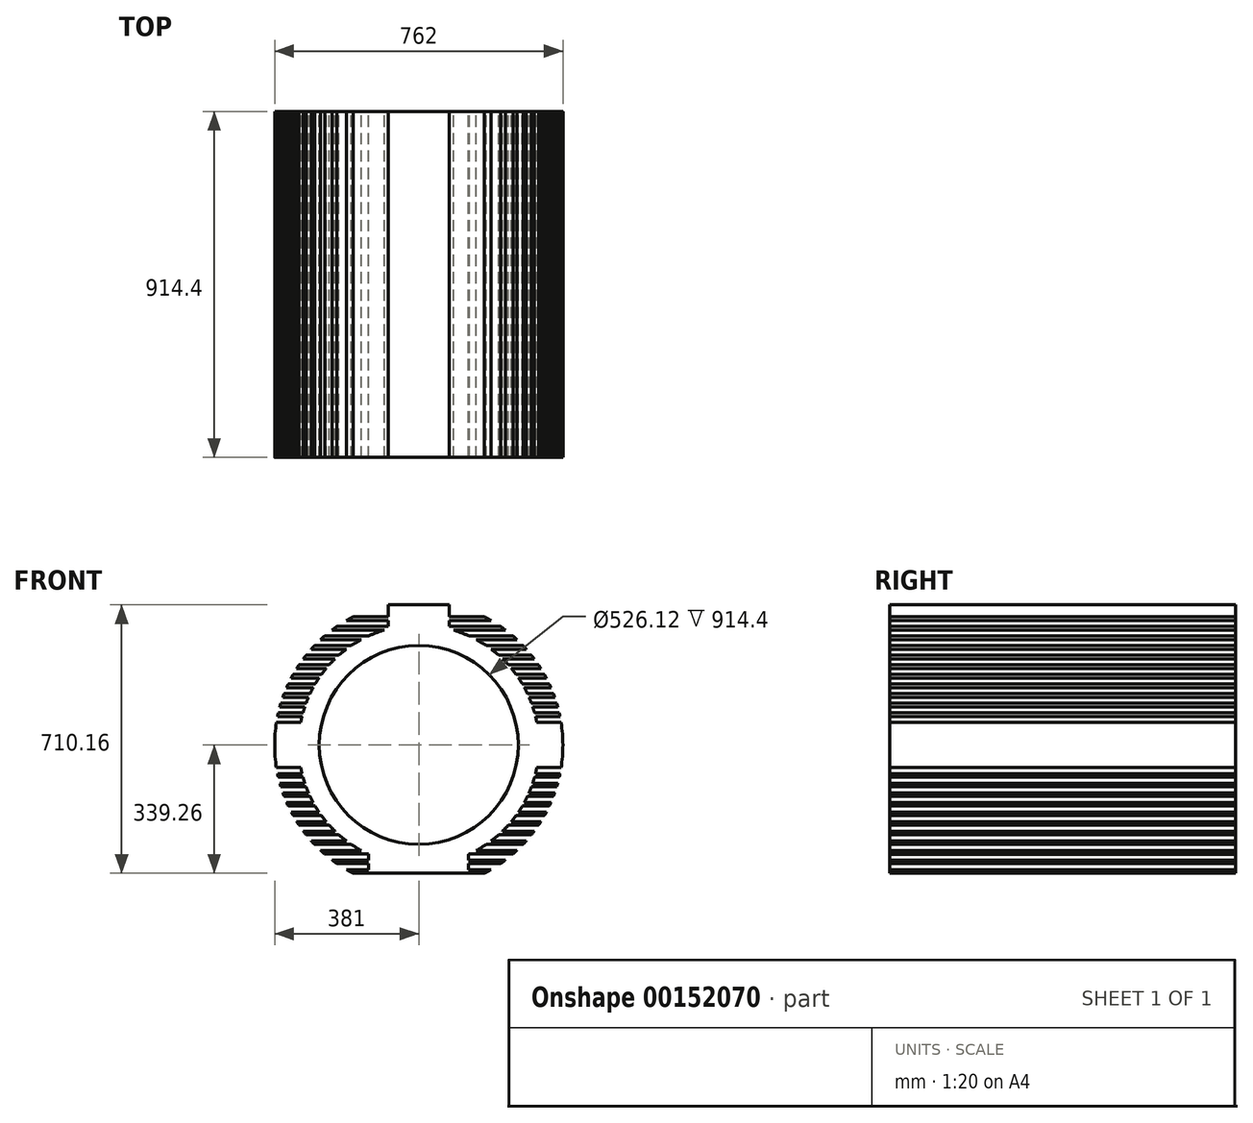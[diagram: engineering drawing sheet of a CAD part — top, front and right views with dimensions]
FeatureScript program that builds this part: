
annotation { "Feature Type Name" : "Feature", "Feature Type Description" : "" }
export const myFeature = defineFeature(function(context is Context, id is Id, definition is map)
    precondition{}
    {
        {
            var Q0;
            Q0=qCreatedBy(makeId("Front.planeOp"),FACE);
            var sketch = newSketch(context, id + "F0", { "sketchPlane" : qUnion([Q0])});
            skArc(sketch, "E0", {"start": v(371.34, -85.26) * mm, "mid": v(372.4, -80.5) * mm, "end": v(373.4, -75.74) * mm});
            skCircle(sketch, "E1", {"center": v(0, 0) * mm, "radius": 317.77 * mm});
            skLineSegment(sketch, "E2.bottom", {"start": v(337.21, 177.34) * mm, "end": v(263.69, 177.34) * mm});
            skLineSegment(sketch, "E2.top", {"start": v(332.03, 186.86) * mm, "end": v(257.02, 186.86) * mm});
            skPoint(sketch, "E2.middle", {"position": v(0, 182.1) * mm});
            skLineSegment(sketch, "E3", {"start": v(0, 470.68) * mm, "end": v(0, -487.75) * mm, "construction": true});
            skLineSegment(sketch, "E4.bottom", {"start": v(322.58, 202.74) * mm, "end": v(244.7, 202.74) * mm});
            skLineSegment(sketch, "E4.top", {"start": v(316.4, 212.26) * mm, "end": v(236.48, 212.26) * mm});
            skLineSegment(sketch, "E5.bottom", {"start": v(305.15, 228.14) * mm, "end": v(221.2, 228.14) * mm});
            skLineSegment(sketch, "E5.top", {"start": v(297.79, 237.66) * mm, "end": v(210.94, 237.66) * mm});
            skLineSegment(sketch, "E6.bottom", {"start": v(284.4, 253.54) * mm, "end": v(191.57, 253.54) * mm});
            skLineSegment(sketch, "E6.top", {"start": v(275.6, 263.06) * mm, "end": v(178.26, 263.06) * mm});
            skLineSegment(sketch, "E7.bottom", {"start": v(259.53, 278.94) * mm, "end": v(152.23, 278.94) * mm});
            skLineSegment(sketch, "E7.top", {"start": v(248.9, 288.46) * mm, "end": v(133.3, 288.46) * mm});
            skLineSegment(sketch, "E8.bottom", {"start": v(229.22, 304.34) * mm, "end": v(91.42, 304.34) * mm});
            skLineSegment(sketch, "E8.top", {"start": v(216, 313.86) * mm, "end": v(80.97, 313.86) * mm});
            skLineSegment(sketch, "E9.bottom", {"start": v(190.88, 329.74) * mm, "end": v(80.97, 329.74) * mm});
            skLineSegment(sketch, "E9.top", {"start": v(173.39, 339.26) * mm, "end": v(80.97, 339.26) * mm});
            skLineSegment(sketch, "E10.bottom", {"start": v(349.4, 151.94) * mm, "end": v(279.1, 151.94) * mm});
            skLineSegment(sketch, "E10.top", {"start": v(345.1, 161.46) * mm, "end": v(273.7, 161.46) * mm});
            skLineSegment(sketch, "E11.bottom", {"start": v(359.37, 126.54) * mm, "end": v(291.5, 126.54) * mm});
            skLineSegment(sketch, "E11.top", {"start": v(355.88, 136.06) * mm, "end": v(287.17, 136.06) * mm});
            skLineSegment(sketch, "E12.bottom", {"start": v(367.33, 101.14) * mm, "end": v(301.25, 101.14) * mm});
            skLineSegment(sketch, "E12.top", {"start": v(364.58, 110.66) * mm, "end": v(297.88, 110.66) * mm});
            skLineSegment(sketch, "E13.bottom", {"start": v(373.4, 75.74) * mm, "end": v(308.61, 75.74) * mm});
            skLineSegment(sketch, "E13.top", {"start": v(371.34, 85.26) * mm, "end": v(306.12, 85.26) * mm});
            skLineSegment(sketch, "E14.trimOffspring", {"start": v(-308.61, 75.74) * mm, "end": v(-373.4, 75.74) * mm});
            skLineSegment(sketch, "E15.trimOffspring", {"start": v(-306.12, 85.26) * mm, "end": v(-371.34, 85.26) * mm});
            skLineSegment(sketch, "E16.trimOffspring", {"start": v(-301.25, 101.14) * mm, "end": v(-367.33, 101.14) * mm});
            skLineSegment(sketch, "E17.trimOffspring", {"start": v(-297.88, 110.66) * mm, "end": v(-364.58, 110.66) * mm});
            skLineSegment(sketch, "E18.trimOffspring", {"start": v(-291.5, 126.54) * mm, "end": v(-359.37, 126.54) * mm});
            skLineSegment(sketch, "E19.trimOffspring", {"start": v(-287.17, 136.06) * mm, "end": v(-355.88, 136.06) * mm});
            skLineSegment(sketch, "E20.trimOffspring", {"start": v(-279.1, 151.94) * mm, "end": v(-349.4, 151.94) * mm});
            skLineSegment(sketch, "E21.trimOffspring", {"start": v(-273.7, 161.46) * mm, "end": v(-345.1, 161.46) * mm});
            skLineSegment(sketch, "E22.trimOffspring", {"start": v(-263.69, 177.34) * mm, "end": v(-337.21, 177.34) * mm});
            skLineSegment(sketch, "E23.trimOffspring", {"start": v(-257.02, 186.86) * mm, "end": v(-332.03, 186.86) * mm});
            skLineSegment(sketch, "E24.trimOffspring", {"start": v(-244.7, 202.74) * mm, "end": v(-322.58, 202.74) * mm});
            skLineSegment(sketch, "E25.trimOffspring", {"start": v(-236.48, 212.26) * mm, "end": v(-316.4, 212.26) * mm});
            skLineSegment(sketch, "E26.trimOffspring", {"start": v(-221.2, 228.14) * mm, "end": v(-305.15, 228.14) * mm});
            skLineSegment(sketch, "E27.trimOffspring", {"start": v(-210.94, 237.66) * mm, "end": v(-297.79, 237.66) * mm});
            skLineSegment(sketch, "E28.trimOffspring", {"start": v(-191.57, 253.54) * mm, "end": v(-284.4, 253.54) * mm});
            skLineSegment(sketch, "E29.trimOffspring", {"start": v(-178.26, 263.06) * mm, "end": v(-275.6, 263.06) * mm});
            skLineSegment(sketch, "E30.trimOffspring", {"start": v(-152.23, 278.94) * mm, "end": v(-259.53, 278.94) * mm});
            skLineSegment(sketch, "E31.trimOffspring", {"start": v(-133.3, 288.46) * mm, "end": v(-248.9, 288.46) * mm});
            skLineSegment(sketch, "E32.trimOffspring", {"start": v(-91.42, 304.34) * mm, "end": v(-229.22, 304.34) * mm});
            skLineSegment(sketch, "E33.trimOffspring", {"start": v(-80.97, 313.86) * mm, "end": v(-216, 313.86) * mm});
            skLineSegment(sketch, "E34", {"start": v(-457.72, 0) * mm, "end": v(505.35, 0) * mm, "construction": true});
            skLineSegment(sketch, "E35.MirrorCS", {"start": v(345.1, -161.46) * mm, "end": v(273.7, -161.46) * mm});
            skLineSegment(sketch, "E36.MirrorCS", {"start": v(-178.26, -263.06) * mm, "end": v(-275.6, -263.06) * mm});
            skLineSegment(sketch, "E37.MirrorCS", {"start": v(-263.69, -177.34) * mm, "end": v(-337.21, -177.34) * mm});
            skLineSegment(sketch, "E38.MirrorCS", {"start": v(-236.48, -212.26) * mm, "end": v(-316.4, -212.26) * mm});
            skLineSegment(sketch, "E39.MirrorCS", {"start": v(-291.5, -126.54) * mm, "end": v(-359.37, -126.54) * mm});
            skLineSegment(sketch, "E40.MirrorCS", {"start": v(-273.7, -161.46) * mm, "end": v(-345.1, -161.46) * mm});
            skPoint(sketch, "E41.MirrorP", {"position": v(0, -182.1) * mm});
            skLineSegment(sketch, "E42.MirrorCS", {"start": v(305.15, -228.14) * mm, "end": v(221.2, -228.14) * mm});
            skLineSegment(sketch, "E43.MirrorCS", {"start": v(-132.08, -313.86) * mm, "end": v(-216, -313.86) * mm});
            skLineSegment(sketch, "E44.MirrorCS", {"start": v(367.33, -101.14) * mm, "end": v(301.25, -101.14) * mm});
            skLineSegment(sketch, "E45.MirrorCS", {"start": v(-297.88, -110.66) * mm, "end": v(-364.58, -110.66) * mm});
            skLineSegment(sketch, "E46.MirrorCS", {"start": v(-257.02, -186.86) * mm, "end": v(-332.03, -186.86) * mm});
            skLineSegment(sketch, "E47.MirrorCS", {"start": v(297.79, -237.66) * mm, "end": v(210.94, -237.66) * mm});
            skLineSegment(sketch, "E48.MirrorCS", {"start": v(284.4, -253.54) * mm, "end": v(191.57, -253.54) * mm});
            skLineSegment(sketch, "E49.MirrorCS", {"start": v(371.34, -85.26) * mm, "end": v(306.12, -85.26) * mm});
            skLineSegment(sketch, "E50.MirrorCS", {"start": v(275.6, -263.06) * mm, "end": v(178.26, -263.06) * mm});
            skLineSegment(sketch, "E51.MirrorCS", {"start": v(-221.2, -228.14) * mm, "end": v(-305.15, -228.14) * mm});
            skLineSegment(sketch, "E52.MirrorCS", {"start": v(355.88, -136.06) * mm, "end": v(287.17, -136.06) * mm});
            skLineSegment(sketch, "E53.MirrorCS", {"start": v(259.53, -278.94) * mm, "end": v(152.23, -278.94) * mm});
            skLineSegment(sketch, "E54.MirrorCS", {"start": v(248.9, -288.46) * mm, "end": v(133.3, -288.46) * mm});
            skLineSegment(sketch, "E55.MirrorCS", {"start": v(-287.17, -136.06) * mm, "end": v(-355.88, -136.06) * mm});
            skLineSegment(sketch, "E56.MirrorCS", {"start": v(173.39, -339.26) * mm, "end": v(-173.39, -339.26) * mm});
            skLineSegment(sketch, "E57.MirrorCS", {"start": v(322.58, -202.74) * mm, "end": v(244.7, -202.74) * mm});
            skLineSegment(sketch, "E58.MirrorCS", {"start": v(332.03, -186.86) * mm, "end": v(257.02, -186.86) * mm});
            skLineSegment(sketch, "E59.MirrorCS", {"start": v(337.21, -177.34) * mm, "end": v(263.69, -177.34) * mm});
            skLineSegment(sketch, "E60.MirrorCS", {"start": v(-308.61, -75.74) * mm, "end": v(-373.4, -75.74) * mm});
            skLineSegment(sketch, "E61.MirrorCS", {"start": v(316.4, -212.26) * mm, "end": v(236.48, -212.26) * mm});
            skLineSegment(sketch, "E62.MirrorCS", {"start": v(373.4, -75.74) * mm, "end": v(308.61, -75.74) * mm});
            skLineSegment(sketch, "E63.MirrorCS", {"start": v(-133.3, -288.46) * mm, "end": v(-248.9, -288.46) * mm});
            skLineSegment(sketch, "E64.MirrorCS", {"start": v(-191.57, -253.54) * mm, "end": v(-284.4, -253.54) * mm});
            skLineSegment(sketch, "E65.MirrorCS", {"start": v(-244.7, -202.74) * mm, "end": v(-322.58, -202.74) * mm});
            skLineSegment(sketch, "E66.MirrorCS", {"start": v(-306.12, -85.26) * mm, "end": v(-371.34, -85.26) * mm});
            skLineSegment(sketch, "E67.MirrorCS", {"start": v(-152.23, -278.94) * mm, "end": v(-259.53, -278.94) * mm});
            skLineSegment(sketch, "E68.MirrorCS", {"start": v(359.37, -126.54) * mm, "end": v(291.5, -126.54) * mm});
            skLineSegment(sketch, "E69.MirrorCS", {"start": v(190.88, -329.74) * mm, "end": v(132.08, -329.74) * mm});
            skLineSegment(sketch, "E70.MirrorCS", {"start": v(349.4, -151.94) * mm, "end": v(279.1, -151.94) * mm});
            skLineSegment(sketch, "E71.MirrorCS", {"start": v(216, -313.86) * mm, "end": v(132.08, -313.86) * mm});
            skLineSegment(sketch, "E72.MirrorCS", {"start": v(229.22, -304.34) * mm, "end": v(132.08, -304.34) * mm});
            skLineSegment(sketch, "E73.MirrorCS", {"start": v(-132.08, -304.34) * mm, "end": v(-229.22, -304.34) * mm});
            skLineSegment(sketch, "E74.MirrorCS", {"start": v(-210.94, -237.66) * mm, "end": v(-297.79, -237.66) * mm});
            skLineSegment(sketch, "E75.MirrorCS", {"start": v(-279.1, -151.94) * mm, "end": v(-349.4, -151.94) * mm});
            skLineSegment(sketch, "E76.MirrorCS", {"start": v(364.58, -110.66) * mm, "end": v(297.88, -110.66) * mm});
            skLineSegment(sketch, "E77.MirrorCS", {"start": v(-301.25, -101.14) * mm, "end": v(-367.33, -101.14) * mm});
            skArc(sketch, "E78.trimOffspring", {"start": v(364.58, -110.66) * mm, "mid": v(365.98, -105.9) * mm, "end": v(367.33, -101.14) * mm});
            skArc(sketch, "E79.trimOffspring", {"start": v(355.88, -136.06) * mm, "mid": v(357.66, -131.31) * mm, "end": v(359.37, -126.54) * mm});
            skArc(sketch, "E80.trimOffspring", {"start": v(345.1, -161.46) * mm, "mid": v(347.28, -156.71) * mm, "end": v(349.4, -151.94) * mm});
            skArc(sketch, "E81.trimOffspring", {"start": v(332.03, -186.86) * mm, "mid": v(334.66, -182.12) * mm, "end": v(337.21, -177.34) * mm});
            skArc(sketch, "E82.trimOffspring", {"start": v(316.4, -212.26) * mm, "mid": v(319.52, -207.52) * mm, "end": v(322.58, -202.74) * mm});
            skArc(sketch, "E83.trimOffspring", {"start": v(297.79, -237.66) * mm, "mid": v(301.5, -232.93) * mm, "end": v(305.15, -228.14) * mm});
            skArc(sketch, "E84.trimOffspring", {"start": v(275.6, -263.06) * mm, "mid": v(280.04, -258.34) * mm, "end": v(284.4, -253.54) * mm});
            skArc(sketch, "E85.trimOffspring", {"start": v(248.9, -288.46) * mm, "mid": v(254.26, -283.75) * mm, "end": v(259.53, -278.94) * mm});
            skArc(sketch, "E86.trimOffspring", {"start": v(216, -313.86) * mm, "mid": v(222.66, -309.17) * mm, "end": v(229.22, -304.34) * mm});
            skArc(sketch, "E87.trimOffspring", {"start": v(173.39, -339.26) * mm, "mid": v(182.2, -334.61) * mm, "end": v(190.88, -329.74) * mm});
            skArc(sketch, "E88.trimOffspring", {"start": v(-229.22, -304.34) * mm, "mid": v(-222.66, -309.17) * mm, "end": v(-216, -313.86) * mm});
            skArc(sketch, "E89.trimOffspring", {"start": v(-259.53, -278.94) * mm, "mid": v(-254.26, -283.75) * mm, "end": v(-248.9, -288.46) * mm});
            skArc(sketch, "E90.trimOffspring", {"start": v(-284.4, -253.54) * mm, "mid": v(-280.04, -258.34) * mm, "end": v(-275.6, -263.06) * mm});
            skArc(sketch, "E91.trimOffspring", {"start": v(-305.15, -228.14) * mm, "mid": v(-301.5, -232.93) * mm, "end": v(-297.79, -237.66) * mm});
            skArc(sketch, "E92.trimOffspring", {"start": v(-322.58, -202.74) * mm, "mid": v(-319.52, -207.52) * mm, "end": v(-316.4, -212.26) * mm});
            skArc(sketch, "E93.trimOffspring", {"start": v(-337.21, -177.34) * mm, "mid": v(-334.66, -182.12) * mm, "end": v(-332.03, -186.86) * mm});
            skArc(sketch, "E94.trimOffspring", {"start": v(-349.4, -151.94) * mm, "mid": v(-347.28, -156.71) * mm, "end": v(-345.1, -161.46) * mm});
            skArc(sketch, "E95.trimOffspring", {"start": v(-359.37, -126.54) * mm, "mid": v(-357.66, -131.31) * mm, "end": v(-355.88, -136.06) * mm});
            skArc(sketch, "E96.trimOffspring", {"start": v(-367.33, -101.14) * mm, "mid": v(-365.98, -105.9) * mm, "end": v(-364.58, -110.66) * mm});
            skArc(sketch, "E97.trimOffspring", {"start": v(-371.34, 85.26) * mm, "mid": v(-372.4, 80.5) * mm, "end": v(-373.4, 75.74) * mm});
            skArc(sketch, "E98.trimOffspring", {"start": v(-364.58, 110.66) * mm, "mid": v(-365.98, 105.9) * mm, "end": v(-367.33, 101.14) * mm});
            skArc(sketch, "E99.trimOffspring", {"start": v(-355.88, 136.06) * mm, "mid": v(-357.66, 131.31) * mm, "end": v(-359.37, 126.54) * mm});
            skArc(sketch, "E100.trimOffspring", {"start": v(-345.1, 161.46) * mm, "mid": v(-347.28, 156.71) * mm, "end": v(-349.4, 151.94) * mm});
            skArc(sketch, "E101.trimOffspring", {"start": v(-332.03, 186.86) * mm, "mid": v(-334.66, 182.12) * mm, "end": v(-337.21, 177.34) * mm});
            skArc(sketch, "E102.trimOffspring", {"start": v(-316.4, 212.26) * mm, "mid": v(-319.52, 207.52) * mm, "end": v(-322.58, 202.74) * mm});
            skArc(sketch, "E103.trimOffspring", {"start": v(-297.79, 237.66) * mm, "mid": v(-301.5, 232.93) * mm, "end": v(-305.15, 228.14) * mm});
            skArc(sketch, "E104.trimOffspring", {"start": v(-275.6, 263.06) * mm, "mid": v(-280.04, 258.34) * mm, "end": v(-284.4, 253.54) * mm});
            skArc(sketch, "E105.trimOffspring", {"start": v(-248.9, 288.46) * mm, "mid": v(-254.26, 283.75) * mm, "end": v(-259.53, 278.94) * mm});
            skArc(sketch, "E106.trimOffspring", {"start": v(-216, 313.86) * mm, "mid": v(-222.66, 309.17) * mm, "end": v(-229.22, 304.34) * mm});
            skArc(sketch, "E107.trimOffspring", {"start": v(-173.39, 339.26) * mm, "mid": v(-182.2, 334.61) * mm, "end": v(-190.88, 329.74) * mm});
            skArc(sketch, "E108.trimOffspring", {"start": v(190.88, 329.74) * mm, "mid": v(182.2, 334.61) * mm, "end": v(173.39, 339.26) * mm});
            skArc(sketch, "E109.trimOffspring", {"start": v(229.22, 304.34) * mm, "mid": v(222.66, 309.17) * mm, "end": v(216, 313.86) * mm});
            skArc(sketch, "E110.trimOffspring", {"start": v(259.53, 278.94) * mm, "mid": v(254.26, 283.75) * mm, "end": v(248.9, 288.46) * mm});
            skArc(sketch, "E111.trimOffspring", {"start": v(284.4, 253.54) * mm, "mid": v(280.04, 258.34) * mm, "end": v(275.6, 263.06) * mm});
            skArc(sketch, "E112.trimOffspring", {"start": v(305.15, 228.14) * mm, "mid": v(301.5, 232.93) * mm, "end": v(297.79, 237.66) * mm});
            skArc(sketch, "E113.trimOffspring", {"start": v(322.58, 202.74) * mm, "mid": v(319.52, 207.52) * mm, "end": v(316.4, 212.26) * mm});
            skArc(sketch, "E114.trimOffspring", {"start": v(337.21, 177.34) * mm, "mid": v(334.66, 182.12) * mm, "end": v(332.03, 186.86) * mm});
            skArc(sketch, "E115.trimOffspring", {"start": v(349.4, 151.94) * mm, "mid": v(347.28, 156.71) * mm, "end": v(345.1, 161.46) * mm});
            skArc(sketch, "E116.trimOffspring", {"start": v(359.37, 126.54) * mm, "mid": v(357.66, 131.31) * mm, "end": v(355.88, 136.06) * mm});
            skArc(sketch, "E117.trimOffspring", {"start": v(367.33, 101.14) * mm, "mid": v(365.98, 105.9) * mm, "end": v(364.58, 110.66) * mm});
            skLineSegment(sketch, "E118", {"start": v(308.61, 75.74) * mm, "end": v(308.61, 59.86) * mm});
            skLineSegment(sketch, "E119", {"start": v(308.61, 59.86) * mm, "end": v(376.27, 59.86) * mm});
            skLineSegment(sketch, "E120", {"start": v(308.61, -75.74) * mm, "end": v(308.61, -59.86) * mm});
            skLineSegment(sketch, "E121", {"start": v(308.61, -59.86) * mm, "end": v(376.27, -59.86) * mm});
            skLineSegment(sketch, "E122", {"start": v(-308.61, 75.74) * mm, "end": v(-308.61, 59.86) * mm});
            skLineSegment(sketch, "E123", {"start": v(-308.61, 59.86) * mm, "end": v(-376.27, 59.86) * mm});
            skLineSegment(sketch, "E124", {"start": v(-308.61, -75.74) * mm, "end": v(-308.61, -59.86) * mm});
            skLineSegment(sketch, "E125", {"start": v(-308.61, -59.86) * mm, "end": v(-376.27, -59.86) * mm});
            skLineSegment(sketch, "E126.bottom", {"start": v(80.97, 370.9) * mm, "end": v(-80.97, 370.9) * mm});
            skLineSegment(sketch, "E126.left", {"start": v(80.97, 370.9) * mm, "end": v(80.97, 307.28) * mm});
            skLineSegment(sketch, "E126.right", {"start": v(-80.97, 370.9) * mm, "end": v(-80.97, 307.28) * mm});
            skPoint(sketch, "E126.middle", {"position": v(0, 329.74) * mm});
            skArc(sketch, "E127.trimOffspring", {"start": v(373.4, 75.74) * mm, "mid": v(372.4, 80.5) * mm, "end": v(371.34, 85.26) * mm});
            skArc(sketch, "E128.trimOffspring", {"start": v(376.27, -59.86) * mm, "mid": v(381, 0) * mm, "end": v(376.27, 59.86) * mm});
            skArc(sketch, "E129.trimOffspring", {"start": v(-373.4, -75.74) * mm, "mid": v(-372.4, -80.5) * mm, "end": v(-371.34, -85.26) * mm});
            skArc(sketch, "E130.trimOffspring", {"start": v(-376.27, 59.86) * mm, "mid": v(-381, 0) * mm, "end": v(-376.27, -59.86) * mm});
            skLineSegment(sketch, "E131.bottom", {"start": v(-132.08, -339.26) * mm, "end": v(132.08, -339.26) * mm});
            skLineSegment(sketch, "E131.left", {"start": v(-132.08, -339.26) * mm, "end": v(-132.08, -289.02) * mm});
            skLineSegment(sketch, "E131.right", {"start": v(132.08, -339.26) * mm, "end": v(132.08, -289.02) * mm});
            skPoint(sketch, "E131.middle", {"position": v(0, -300.25) * mm});
            skArc(sketch, "E132.trimOffspring", {"start": v(-190.88, -329.74) * mm, "mid": v(-182.2, -334.61) * mm, "end": v(-173.39, -339.26) * mm});
            skPoint(sketch, "E133.orphan", {"position": v(132.08, -261.25) * mm});
            skPoint(sketch, "E134.orphan", {"position": v(-132.08, -261.25) * mm});
            skPoint(sketch, "E135.orphan", {"position": v(49.7, -313.86) * mm});
            skPoint(sketch, "E136.orphan", {"position": v(91.42, -304.34) * mm});
            skLineSegment(sketch, "E137.trimOffspring", {"start": v(-132.08, -329.74) * mm, "end": v(-190.88, -329.74) * mm});
            skPoint(sketch, "E138.orphan", {"position": v(-49.7, -313.86) * mm});
            skPoint(sketch, "E139.orphan", {"position": v(-91.42, -304.34) * mm});
            skLineSegment(sketch, "E140.trimOffspring", {"start": v(-80.97, 339.26) * mm, "end": v(-173.39, 339.26) * mm});
            skLineSegment(sketch, "E141.trimOffspring", {"start": v(-80.97, 329.74) * mm, "end": v(-190.88, 329.74) * mm});
            skPoint(sketch, "E142.orphan", {"position": v(49.7, 313.86) * mm});
            skPoint(sketch, "E143.orphan", {"position": v(-49.7, 313.86) * mm});
            skPoint(sketch, "E144.orphan", {"position": v(80.97, 288.57) * mm});
            skPoint(sketch, "E145.orphan", {"position": v(-80.97, 288.57) * mm});
            skCircle(sketch, "E146", {"center": v(0, 0) * mm, "radius": 263.06 * mm});
            skSolve(sketch);
        }
        {
            var Q0;
            Q0 = qSketchRegion(id + "F0", true);
            extrude(context, id + "F1", {"entities" : qUnion([Q0]), "depth" : 914.4 * mm});
        }
    });
